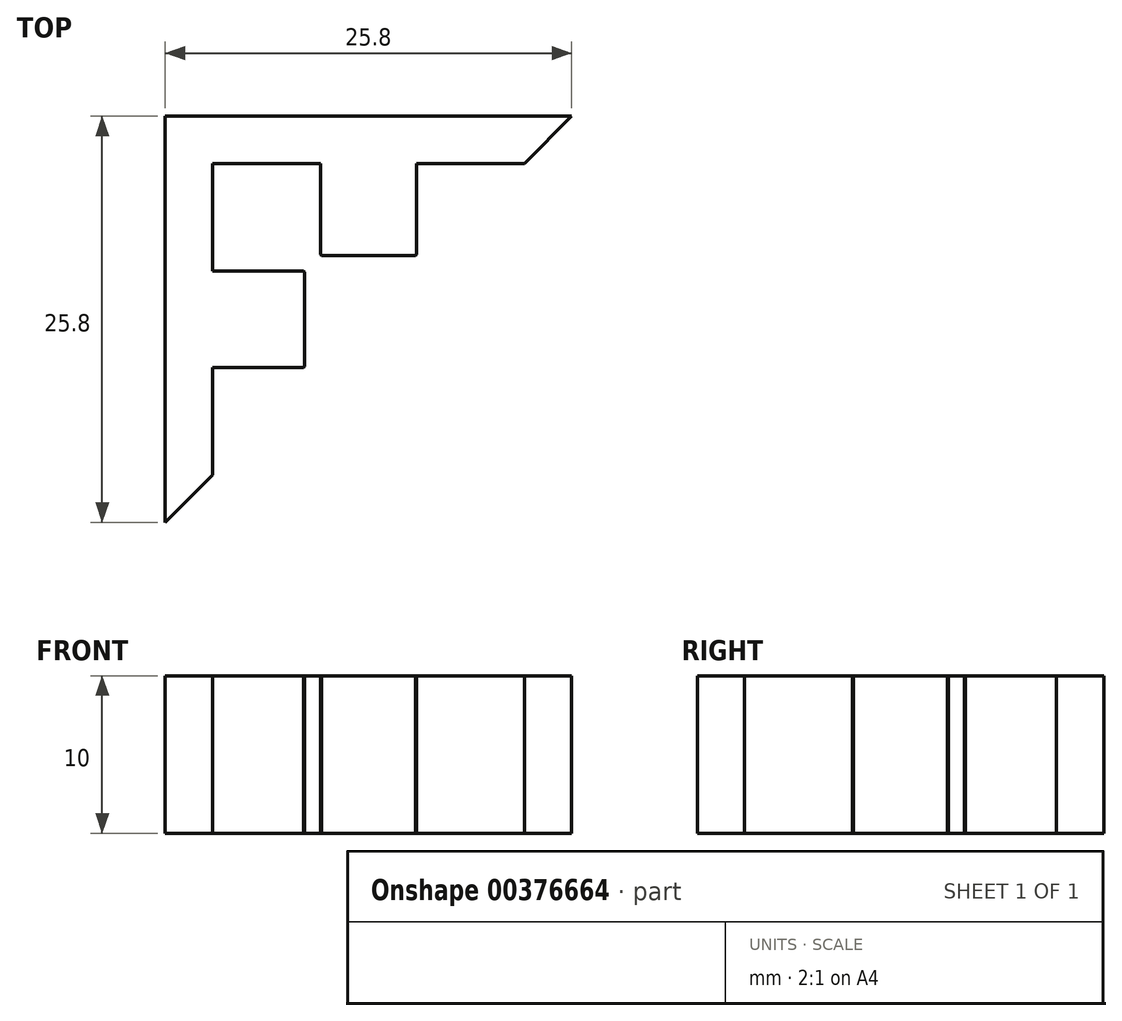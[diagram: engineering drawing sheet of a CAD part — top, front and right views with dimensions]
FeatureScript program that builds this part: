
annotation { "Feature Type Name" : "Feature", "Feature Type Description" : "" }
export const myFeature = defineFeature(function(context is Context, id is Id, definition is map)
    precondition{}
    {
        {
            var Q0;
            Q0=qCreatedBy(makeId("Top.planeOp"),FACE);
            var sketch = newSketch(context, id + "F0", { "sketchPlane" : qUnion([Q0])});
            skLineSegment(sketch, "E0.2.7", {"start": v(-3.15, 8) * mm, "end": v(-3.15, 9.9) * mm});
            skLineSegment(sketch, "E0.2.10", {"start": v(-9.9, 9.9) * mm, "end": v(-3.15, 9.9) * mm});
            skLineSegment(sketch, "E0.2.12", {"start": v(-7.08, 8) * mm, "end": v(-3.15, 8) * mm});
            skLineSegment(sketch, "E0.3.2", {"start": v(-9.9, 3.15) * mm, "end": v(-9.9, 9.9) * mm});
            skLineSegment(sketch, "E0.3.5", {"start": v(-8, 3.15) * mm, "end": v(-9.9, 3.15) * mm});
            skLineSegment(sketch, "E0.anchor2", {"start": v(-3.95, 3.95) * mm, "end": v(-9.9, 9.9) * mm, "construction": true});
            skLineSegment(sketch, "E1.trimOffspring", {"start": v(-8, 3.15) * mm, "end": v(-8, 7.08) * mm});
            skLineSegment(sketch, "E2.1", {"start": v(-16.3, -67.74) * mm, "end": v(-16.3, -67.74) * mm});
            skLineSegment(sketch, "E3", {"start": v(-8, 7.08) * mm, "end": v(-4.07, 3.15) * mm});
            skLineSegment(sketch, "E4.trimOffspring", {"start": v(-3.15, 4.07) * mm, "end": v(-7.08, 8) * mm});
            skLineSegment(sketch, "E5.bottom", {"start": v(-12.9, 12.9) * mm, "end": v(0, 12.9) * mm});
            skLineSegment(sketch, "E6.trimOffspring", {"start": v(-3.15, 9.9) * mm, "end": v(-9.9, 9.9) * mm});
            skLineSegment(sketch, "E7.1", {"start": v(67.73, -66.73) * mm, "end": v(67.73, -66.73) * mm});
            skLineSegment(sketch, "E8", {"start": v(-8, 0) * mm, "end": v(0, 0) * mm, "construction": true});
            skLineSegment(sketch, "E9", {"start": v(0, 0) * mm, "end": v(0, 8) * mm, "construction": true});
            skLineSegment(sketch, "E10", {"start": v(-3.15, 8) * mm, "end": v(0, 8) * mm, "construction": true});
            skLineSegment(sketch, "E11", {"start": v(-8, 3.15) * mm, "end": v(-8, 0) * mm, "construction": true});
            skLineSegment(sketch, "E12", {"start": v(-8, 7.08) * mm, "end": v(-8, 8) * mm, "construction": true});
            skLineSegment(sketch, "E13", {"start": v(-7.08, 8) * mm, "end": v(-8, 8) * mm, "construction": true});
            skLineSegment(sketch, "E14.top", {"start": v(0, 3.95) * mm, "end": v(-3.03, 3.95) * mm});
            skLineSegment(sketch, "E14.right", {"start": v(-3.95, 0) * mm, "end": v(-3.95, 3.03) * mm});
            skLineSegment(sketch, "E15", {"start": v(-12.9, 12.9) * mm, "end": v(-12.9, 0) * mm});
            skArc(sketch, "E16", {"start": v(0, 2.15) * mm, "mid": v(-1.52, 1.52) * mm, "end": v(-2.15, 0) * mm});
            skLineSegment(sketch, "E17.2.7", {"start": v(61.06, 8) * mm, "end": v(61.06, 9.9) * mm});
            skLineSegment(sketch, "E17.2.10", {"start": v(54.3, 9.9) * mm, "end": v(61.06, 9.9) * mm});
            skLineSegment(sketch, "E17.2.12", {"start": v(57.12, 8) * mm, "end": v(61.06, 8) * mm});
            skLineSegment(sketch, "E17.3.2", {"start": v(54.3, 3.15) * mm, "end": v(54.3, 9.9) * mm});
            skLineSegment(sketch, "E17.3.5", {"start": v(56.2, 3.15) * mm, "end": v(54.3, 3.15) * mm});
            skLineSegment(sketch, "E17.anchor2", {"start": v(60.5, 3.7) * mm, "end": v(54.3, 9.9) * mm, "construction": true});
            skLineSegment(sketch, "E18.trimOffspring", {"start": v(56.2, 3.15) * mm, "end": v(56.2, 7.08) * mm});
            skLineSegment(sketch, "E19", {"start": v(56.2, 7.08) * mm, "end": v(60.5, 2.78) * mm});
            skLineSegment(sketch, "E20.trimOffspring", {"start": v(61.42, 3.7) * mm, "end": v(57.12, 8) * mm});
            skLineSegment(sketch, "E21.bottom", {"start": v(51.3, 12.9) * mm, "end": v(64.2, 12.9) * mm});
            skLineSegment(sketch, "E22.trimOffspring", {"start": v(61.06, 9.9) * mm, "end": v(54.3, 9.9) * mm});
            skLineSegment(sketch, "E23", {"start": v(56.2, 0) * mm, "end": v(64.2, 0) * mm, "construction": true});
            skLineSegment(sketch, "E24", {"start": v(64.2, 0) * mm, "end": v(64.2, 8) * mm, "construction": true});
            skLineSegment(sketch, "E25", {"start": v(61.06, 8) * mm, "end": v(64.2, 8) * mm, "construction": true});
            skLineSegment(sketch, "E26", {"start": v(56.2, 3.15) * mm, "end": v(56.2, 0) * mm, "construction": true});
            skLineSegment(sketch, "E27", {"start": v(56.2, 7.08) * mm, "end": v(56.2, 8) * mm, "construction": true});
            skLineSegment(sketch, "E28", {"start": v(57.12, 8) * mm, "end": v(56.2, 8) * mm, "construction": true});
            skLineSegment(sketch, "E29.top", {"start": v(64.2, 3.7) * mm, "end": v(61.42, 3.7) * mm});
            skLineSegment(sketch, "E29.right", {"start": v(60.5, 0) * mm, "end": v(60.5, 2.78) * mm});
            skLineSegment(sketch, "E30", {"start": v(51.3, 12.9) * mm, "end": v(51.3, 0) * mm});
            skArc(sketch, "E31", {"start": v(64.2, 2.15) * mm, "mid": v(62.69, 1.52) * mm, "end": v(62.06, 0) * mm});
            skLineSegment(sketch, "E32.1.0", {"start": v(-12.9, -12.9) * mm, "end": v(0, -12.9) * mm});
            skLineSegment(sketch, "E32.1.1", {"start": v(-8, -3.15) * mm, "end": v(-8, 0) * mm, "construction": true});
            skLineSegment(sketch, "E32.1.2", {"start": v(-3.95, 0) * mm, "end": v(-3.95, -3.03) * mm});
            skLineSegment(sketch, "E32.1.3", {"start": v(-3.15, -8) * mm, "end": v(0, -8) * mm, "construction": true});
            skLineSegment(sketch, "E32.1.4", {"start": v(-8, -3.15) * mm, "end": v(-9.9, -3.15) * mm});
            skLineSegment(sketch, "E32.1.5", {"start": v(-8, -7.08) * mm, "end": v(-8, -3.15) * mm});
            skLineSegment(sketch, "E32.1.6", {"start": v(-3.15, -9.9) * mm, "end": v(-9.9, -9.9) * mm});
            skLineSegment(sketch, "E32.1.7", {"start": v(-3.15, -8) * mm, "end": v(-3.15, -9.9) * mm});
            skLineSegment(sketch, "E32.1.8", {"start": v(-3.95, -3.95) * mm, "end": v(-9.9, -9.9) * mm, "construction": true});
            skLineSegment(sketch, "E32.1.9", {"start": v(-3.15, -8) * mm, "end": v(-7.08, -8) * mm});
            skLineSegment(sketch, "E32.1.10", {"start": v(-7.08, -8) * mm, "end": v(-3.03, -3.95) * mm});
            skLineSegment(sketch, "E32.1.11", {"start": v(-4.07, -3.15) * mm, "end": v(-8, -7.08) * mm});
            skLineSegment(sketch, "E32.1.12", {"start": v(-12.9, -12.9) * mm, "end": v(-12.9, 0) * mm});
            skLineSegment(sketch, "E32.1.13", {"start": v(-9.9, -3.15) * mm, "end": v(-9.9, -9.9) * mm});
            skLineSegment(sketch, "E32.1.14", {"start": v(0, -8) * mm, "end": v(0, 0) * mm, "construction": true});
            skLineSegment(sketch, "E32.1.15", {"start": v(0, 0) * mm, "end": v(-8, 0) * mm, "construction": true});
            skArc(sketch, "E32.1.16", {"start": v(-2.15, 0) * mm, "mid": v(-1.52, -1.52) * mm, "end": v(0, -2.15) * mm});
            skLineSegment(sketch, "E32.1.17", {"start": v(0, -3.95) * mm, "end": v(-3.03, -3.95) * mm});
            skLineSegment(sketch, "E32.1.18", {"start": v(-9.9, -9.9) * mm, "end": v(-9.9, -3.15) * mm});
            skLineSegment(sketch, "E32.1.19", {"start": v(-7.08, -8) * mm, "end": v(-8, -8) * mm, "construction": true});
            skLineSegment(sketch, "E32.1.20", {"start": v(-8, -7.08) * mm, "end": v(-8, -8) * mm, "construction": true});
            skLineSegment(sketch, "E32.2.0", {"start": v(12.9, -12.9) * mm, "end": v(12.9, 0) * mm});
            skLineSegment(sketch, "E32.2.1", {"start": v(3.15, -8) * mm, "end": v(0, -8) * mm, "construction": true});
            skLineSegment(sketch, "E32.2.2", {"start": v(0, -3.95) * mm, "end": v(3.03, -3.95) * mm});
            skLineSegment(sketch, "E32.2.3", {"start": v(8, -3.15) * mm, "end": v(8, 0) * mm, "construction": true});
            skLineSegment(sketch, "E32.2.4", {"start": v(3.15, -8) * mm, "end": v(3.15, -9.9) * mm});
            skLineSegment(sketch, "E32.2.5", {"start": v(7.08, -8) * mm, "end": v(3.15, -8) * mm});
            skLineSegment(sketch, "E32.2.6", {"start": v(9.9, -3.15) * mm, "end": v(9.9, -9.9) * mm});
            skLineSegment(sketch, "E32.2.7", {"start": v(8, -3.15) * mm, "end": v(9.9, -3.15) * mm});
            skLineSegment(sketch, "E32.2.8", {"start": v(3.95, -3.95) * mm, "end": v(9.9, -9.9) * mm, "construction": true});
            skLineSegment(sketch, "E32.2.9", {"start": v(8, -3.15) * mm, "end": v(8, -7.08) * mm});
            skLineSegment(sketch, "E32.2.10", {"start": v(8, -7.08) * mm, "end": v(3.95, -3.03) * mm});
            skLineSegment(sketch, "E32.2.11", {"start": v(3.03, -3.95) * mm, "end": v(7.08, -8) * mm});
            skLineSegment(sketch, "E32.2.12", {"start": v(12.9, -12.9) * mm, "end": v(0, -12.9) * mm});
            skLineSegment(sketch, "E32.2.13", {"start": v(3.15, -9.9) * mm, "end": v(9.9, -9.9) * mm});
            skLineSegment(sketch, "E32.2.14", {"start": v(8, 0) * mm, "end": v(0, 0) * mm, "construction": true});
            skLineSegment(sketch, "E32.2.15", {"start": v(0, 0) * mm, "end": v(0, -8) * mm, "construction": true});
            skArc(sketch, "E32.2.16", {"start": v(0, -2.15) * mm, "mid": v(1.52, -1.52) * mm, "end": v(2.15, 0) * mm});
            skLineSegment(sketch, "E32.2.17", {"start": v(3.95, 0) * mm, "end": v(3.95, -3.03) * mm});
            skLineSegment(sketch, "E32.2.18", {"start": v(9.9, -9.9) * mm, "end": v(3.15, -9.9) * mm});
            skLineSegment(sketch, "E32.2.19", {"start": v(8, -7.08) * mm, "end": v(8, -8) * mm, "construction": true});
            skLineSegment(sketch, "E32.2.20", {"start": v(7.08, -8) * mm, "end": v(8, -8) * mm, "construction": true});
            skLineSegment(sketch, "E32.3.0", {"start": v(12.9, 12.9) * mm, "end": v(0, 12.9) * mm});
            skLineSegment(sketch, "E32.3.1", {"start": v(8, 3.15) * mm, "end": v(8, 0) * mm, "construction": true});
            skLineSegment(sketch, "E32.3.2", {"start": v(3.95, 0) * mm, "end": v(3.95, 3.03) * mm});
            skLineSegment(sketch, "E32.3.3", {"start": v(3.15, 8) * mm, "end": v(0, 8) * mm, "construction": true});
            skLineSegment(sketch, "E32.3.4", {"start": v(8, 3.15) * mm, "end": v(9.9, 3.15) * mm});
            skLineSegment(sketch, "E32.3.5", {"start": v(8, 7.08) * mm, "end": v(8, 3.15) * mm});
            skLineSegment(sketch, "E32.3.6", {"start": v(3.15, 9.9) * mm, "end": v(9.9, 9.9) * mm});
            skLineSegment(sketch, "E32.3.7", {"start": v(3.15, 8) * mm, "end": v(3.15, 9.9) * mm});
            skLineSegment(sketch, "E32.3.8", {"start": v(3.95, 3.95) * mm, "end": v(9.9, 9.9) * mm, "construction": true});
            skLineSegment(sketch, "E32.3.9", {"start": v(3.15, 8) * mm, "end": v(7.08, 8) * mm});
            skLineSegment(sketch, "E32.3.10", {"start": v(7.08, 8) * mm, "end": v(3.15, 4.07) * mm});
            skLineSegment(sketch, "E32.3.11", {"start": v(3.95, 3.03) * mm, "end": v(8, 7.08) * mm});
            skLineSegment(sketch, "E32.3.12", {"start": v(12.9, 12.9) * mm, "end": v(12.9, 0) * mm});
            skLineSegment(sketch, "E32.3.13", {"start": v(9.9, 3.15) * mm, "end": v(9.9, 9.9) * mm});
            skLineSegment(sketch, "E32.3.14", {"start": v(0, 8) * mm, "end": v(0, 0) * mm, "construction": true});
            skLineSegment(sketch, "E32.3.15", {"start": v(0, 0) * mm, "end": v(8, 0) * mm, "construction": true});
            skArc(sketch, "E32.3.16", {"start": v(2.15, 0) * mm, "mid": v(1.52, 1.52) * mm, "end": v(0, 2.15) * mm});
            skLineSegment(sketch, "E32.3.17", {"start": v(0, 3.95) * mm, "end": v(3.03, 3.95) * mm});
            skLineSegment(sketch, "E32.3.18", {"start": v(9.9, 9.9) * mm, "end": v(9.9, 3.15) * mm});
            skLineSegment(sketch, "E32.3.19", {"start": v(7.08, 8) * mm, "end": v(8, 8) * mm, "construction": true});
            skLineSegment(sketch, "E32.3.20", {"start": v(8, 7.08) * mm, "end": v(8, 8) * mm, "construction": true});
            skLineSegment(sketch, "E33", {"start": v(12.9, 12.9) * mm, "end": v(-12.9, -12.9) * mm});
            skLineSegment(sketch, "E34", {"start": v(-8, 3.15) * mm, "end": v(-4.07, 3.15) * mm});
            skLineSegment(sketch, "E35", {"start": v(-8, -3.15) * mm, "end": v(-4.07, -3.15) * mm});
            skLineSegment(sketch, "E36", {"start": v(-3.15, 8) * mm, "end": v(-3.15, 4.07) * mm});
            skLineSegment(sketch, "E37", {"start": v(3.15, 8) * mm, "end": v(3.15, 4.07) * mm});
            skCircle(sketch, "E38", {"center": v(0, 0) * mm, "radius": 3.95 * mm, "construction": true});
            skLineSegment(sketch, "E39", {"start": v(-4.07, -3.15) * mm, "end": v(-3.95, -3.03) * mm});
            skLineSegment(sketch, "E40", {"start": v(-4.07, 3.15) * mm, "end": v(-3.95, 3.03) * mm});
            skLineSegment(sketch, "E41", {"start": v(-3.15, 4.07) * mm, "end": v(-3.03, 3.95) * mm});
            skLineSegment(sketch, "E42", {"start": v(3.03, 3.95) * mm, "end": v(3.15, 4.07) * mm});
            skLineSegment(sketch, "E43.0", {"start": v(-3.05, 8) * mm, "end": v(-3.05, 9.9) * mm});
            skLineSegment(sketch, "E43.1", {"start": v(-3.05, 8) * mm, "end": v(-3.05, 4.11) * mm});
            skLineSegment(sketch, "E43.2", {"start": v(-3.05, 4.11) * mm, "end": v(-2.99, 4.05) * mm});
            skLineSegment(sketch, "E43.3", {"start": v(0, 4.05) * mm, "end": v(-2.99, 4.05) * mm});
            skLineSegment(sketch, "E43.4", {"start": v(3.05, 8) * mm, "end": v(3.05, 9.9) * mm});
            skLineSegment(sketch, "E43.5", {"start": v(3.05, 8) * mm, "end": v(3.05, 4.11) * mm});
            skLineSegment(sketch, "E43.6", {"start": v(2.99, 4.05) * mm, "end": v(3.05, 4.11) * mm});
            skLineSegment(sketch, "E43.7", {"start": v(0, 4.05) * mm, "end": v(2.99, 4.05) * mm});
            skLineSegment(sketch, "E44", {"start": v(-3.05, 9.9) * mm, "end": v(-3.15, 9.9) * mm});
            skLineSegment(sketch, "E45", {"start": v(3.05, 9.9) * mm, "end": v(3.15, 9.9) * mm});
            skLineSegment(sketch, "E46.0", {"start": v(-8, 3.05) * mm, "end": v(-9.9, 3.05) * mm});
            skLineSegment(sketch, "E46.1", {"start": v(-8, 3.05) * mm, "end": v(-4.11, 3.05) * mm});
            skLineSegment(sketch, "E46.2", {"start": v(-4.11, 3.05) * mm, "end": v(-4.05, 2.99) * mm});
            skLineSegment(sketch, "E46.3", {"start": v(-4.05, 0) * mm, "end": v(-4.05, 2.99) * mm});
            skLineSegment(sketch, "E46.4", {"start": v(-8, -3.05) * mm, "end": v(-9.9, -3.05) * mm});
            skLineSegment(sketch, "E46.5", {"start": v(-8, -3.05) * mm, "end": v(-4.11, -3.05) * mm});
            skLineSegment(sketch, "E46.6", {"start": v(-4.11, -3.05) * mm, "end": v(-4.05, -2.99) * mm});
            skLineSegment(sketch, "E46.7", {"start": v(-4.05, 0) * mm, "end": v(-4.05, -2.99) * mm});
            skLineSegment(sketch, "E47", {"start": v(-9.9, 3.15) * mm, "end": v(-9.9, 3.05) * mm});
            skLineSegment(sketch, "E48", {"start": v(-9.9, -3.15) * mm, "end": v(-9.9, -3.05) * mm});
            skSolve(sketch);
        }
        {
            var Q0;
            Q0=makeQuery(id+"F0.imprint","IMPRINT",FACE,{"disambiguationData":[TD([[makeQuery(id+"F0.imprint","IMPRINT",EDGE,{"derivedFrom":sQuery(id+"F0.wireOp",EDGE,"E0.3.2")}),1.0]])]});
            extrude(context, id + "F1", {"entities" : qUnion([Q0]), "depth" : 10 * mm, "offsetDistance" : 25 * mm});
        }
    });
